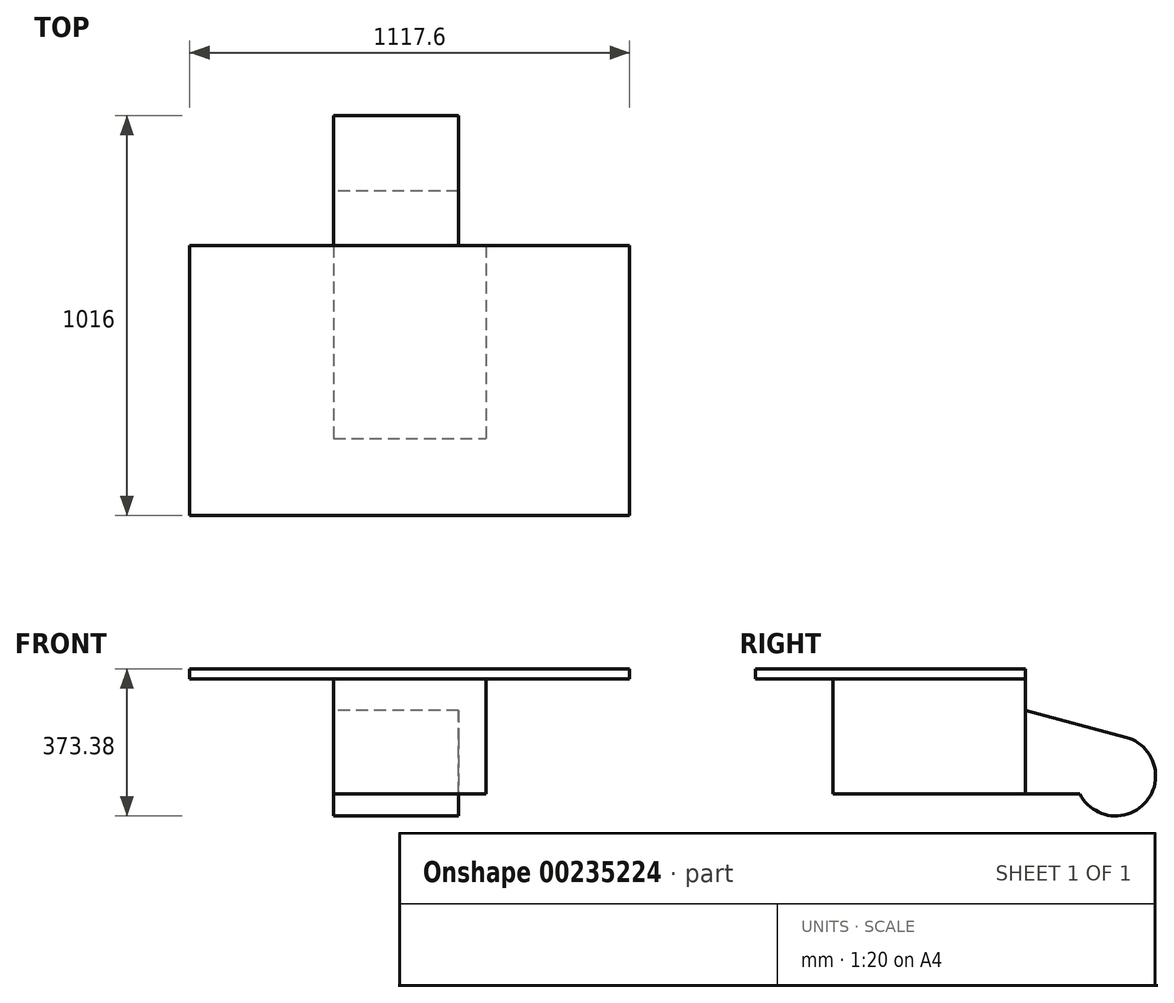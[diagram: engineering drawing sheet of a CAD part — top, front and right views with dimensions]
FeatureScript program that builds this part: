
annotation { "Feature Type Name" : "Feature", "Feature Type Description" : "" }
export const myFeature = defineFeature(function(context is Context, id is Id, definition is map)
    precondition{}
    {
        {
            var Q0;
            Q0=qCreatedBy(makeId("Top.planeOp"),FACE);
            var sketch = newSketch(context, id + "F0", { "sketchPlane" : qUnion([Q0])});
            skLineSegment(sketch, "E0.bottom", {"start": v(-558.8, 342.9) * mm, "end": v(558.8, 342.9) * mm});
            skLineSegment(sketch, "E0.top", {"start": v(-558.8, -342.9) * mm, "end": v(558.8, -342.9) * mm});
            skLineSegment(sketch, "E0.left", {"start": v(-558.8, 342.9) * mm, "end": v(-558.8, -342.9) * mm});
            skLineSegment(sketch, "E0.right", {"start": v(558.8, 342.9) * mm, "end": v(558.8, -342.9) * mm});
            skSolve(sketch);
        }
        {
            var Q0;
            Q0=makeQuery(id+"F0.imprint","IMPRINT",FACE,{"disambiguationData":[TD([[makeQuery(id+"F0.imprint","IMPRINT",EDGE,{"derivedFrom":sQuery(id+"F0.wireOp",EDGE,"E0.bottom")}),-1.0]])]});
            extrude(context, id + "F1", {"entities" : qUnion([Q0]), "oppositeDirection" : true, "depth" : 25.4 * mm});
        }
        {
            var Q0;
            Q0=makeQuery(id+"F1.opExtrude","CAP_FACE",FACE,{"disambiguationData":[OSD([sQuery(id+"F0.wireOp",EDGE,"E0.bottom"),sQuery(id+"F0.wireOp",EDGE,"E0.top"),sQuery(id+"F0.wireOp",EDGE,"E0.left"),sQuery(id+"F0.wireOp",EDGE,"E0.right")])],"isStart":false});
            var sketch = newSketch(context, id + "F2", { "sketchPlane" : qUnion([Q0])});
            skLineSegment(sketch, "E1.bottom", {"start": v(-193.68, -342.9) * mm, "end": v(193.68, -342.9) * mm});
            skLineSegment(sketch, "E1.top", {"start": v(-193.67, 146.81) * mm, "end": v(193.67, 146.81) * mm});
            skLineSegment(sketch, "E1.left", {"start": v(-193.68, -342.9) * mm, "end": v(-193.67, 146.81) * mm});
            skLineSegment(sketch, "E1.right", {"start": v(193.67, -342.9) * mm, "end": v(193.68, 146.81) * mm});
            skSolve(sketch);
        }
        {
            var Q0;
            Q0=makeQuery(id+"F2.imprint","IMPRINT",FACE,{"disambiguationData":[TD([[makeQuery(id+"F2.imprint","IMPRINT",EDGE,{"derivedFrom":sQuery(id+"F2.wireOp",EDGE,"E1.bottom")}),1.0]])]});
            extrude(context, id + "F3", {"entities" : qUnion([Q0]), "operationType" : NewBodyOperationType.ADD, "depth" : 292.1 * mm});
        }
        {
            var Q0;
            Q0=makeQuery(id+"F3.opExtrude","SWEPT_FACE",FACE,{"disambiguationData":[OSD([sQuery(id+"F2.wireOp",EDGE,"E1.left")])]});
            var sketch = newSketch(context, id + "F4", { "sketchPlane" : qUnion([Q0])});
            skArc(sketch, "E2", {"start": v(-597.8, -173.64) * mm, "mid": v(-650.31, -335.9) * mm, "end": v(-480.77, -317.5) * mm});
            skLineSegment(sketch, "E3", {"start": v(-342.9, -317.5) * mm, "end": v(-480.77, -317.5) * mm});
            skLineSegment(sketch, "E4", {"start": v(-342.9, -105.34) * mm, "end": v(-597.8, -173.64) * mm});
            skPoint(sketch, "E5", {"position": v(-342.9, -171.45) * mm});
            skSolve(sketch);
        }
        {
            var Q0;
            Q0=makeQuery(id+"F4.imprint","IMPRINT",FACE,{"disambiguationData":[TD([[makeQuery(id+"F4.imprint","IMPRINT",EDGE,{"derivedFrom":sQuery(id+"F4.wireOp",EDGE,"E2")}),1.0]])]});
            extrude(context, id + "F5", {"entities" : qUnion([Q0]), "operationType" : NewBodyOperationType.ADD, "oppositeDirection" : true, "depth" : 317.5 * mm});
        }
    });
